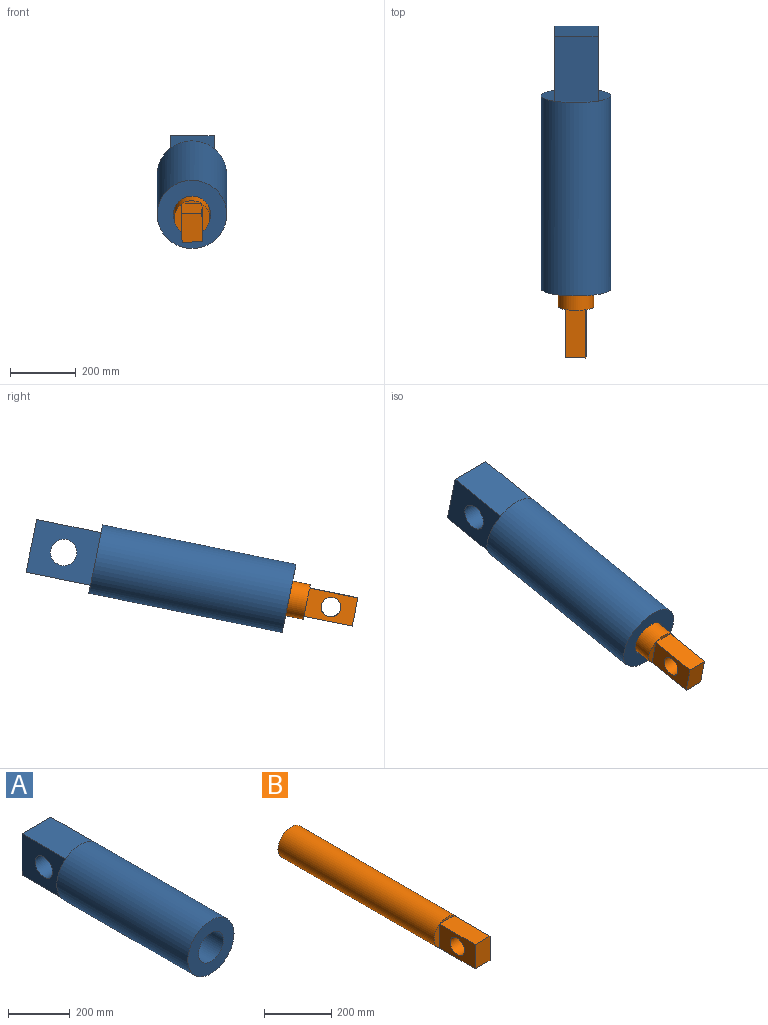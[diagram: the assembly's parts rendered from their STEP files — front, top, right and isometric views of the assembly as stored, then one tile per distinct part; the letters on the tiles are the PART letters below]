
ASSEMBLY  parts=2 mates=1
PART A: 12 faces, bbox 211.7x800x211.7 mm
  f0: plane 211.67x172.93mm, normal (0,1,0), area 9168.8mm2, adj f3,f5,f7,f9
  f1: cylinder r=56.79mm len=600mm, axis (0,1,0), area 214107.9mm2, adj f4,f10
  f2: plane 163.71x38.74mm, normal (0,1,0), area 4412.4mm2, adj f3,f6
  f3: cylinder r=105.84mm len=600mm, axis (0,1,0), area 398997.1mm2, adj f0,f2,f4
  f4: plane 211.67x211.67mm, normal (0,-1,0), area 25057.3mm2, adj f1,f3
  f5: plane 200x132mm, normal (0,0,1), area 26400mm2, adj f0,f6,f8,f9
  f6: plane 200x163.71mm, normal (1,0,0), area 27715.1mm2, adj f2,f5,f7,f8,f11
  f7: plane 200x132mm, normal (0,0,-1), area 26400mm2, adj f0,f6,f8,f9
  f8: plane 163.71x132mm, normal (0,1,0), area 21609.5mm2, adj f5,f6,f7,f9
  f9: plane 200x163.71mm, normal (-1,0,0), area 27715.1mm2, adj f0,f5,f7,f8,f11
  f10: plane 113.59x113.59mm, normal (0,-1,0), area 10133.3mm2, adj f1
  f11: cylinder r=40mm len=132mm, axis (-1,0,0), area 33175.2mm2, adj f6,f9
PART B: 12 faces, bbox 107.3x805x107.3 mm
  f0: plane 87.67x22.72mm, normal (0,-1,0), area 1396.9mm2, adj f3,f6
  f1: plane 61.85x9.81mm, normal (0,-1,0), area 412.6mm2, adj f3,f9
  f2: plane 87.67x22.72mm, normal (0,-1,0), area 1396.9mm2, adj f3,f8
  f3: cylinder r=53.65mm len=655.04mm, axis (0,1,0), area 220798.8mm2, adj f0,f1,f2,f4,f5
  f4: plane 107.29x107.29mm, normal (0,1,0), area 9041.5mm2, adj f3
  f5: plane 61.85x9.81mm, normal (0,-1,0), area 412.6mm2, adj f3,f7
  f6: plane 150x87.67mm, normal (1,0,0), area 10323.5mm2, adj f0,f7,f9,f10,f11
  f7: plane 150x61.85mm, normal (0,0,1), area 9277.6mm2, adj f5,f6,f8,f10
  f8: plane 150x87.67mm, normal (-1,0,0), area 10323.5mm2, adj f2,f7,f9,f10,f11
  f9: plane 150x61.85mm, normal (0,0,-1), area 9277.6mm2, adj f1,f6,f8,f10
  f10: plane 87.67x61.85mm, normal (0,-1,0), area 5422.6mm2, adj f6,f7,f8,f9
  f11: cylinder r=30mm len=61.85mm, axis (-1,0,0), area 11658.6mm2, adj f6,f8
PLACE A rot(axis=(1,0,0),11.5deg) t=(-0.2,-133.01,-202.47)mm fixed
PLACE B rot(axis=(1,-0.07,-0.01),11.6deg) t=(-0.2,405.88,-92.57)mm
MATE cylindrical A.f3 <-> B.f3  axis (0,-0.98,-0.2) through (-0.2,-182.01,-212.46)mm
